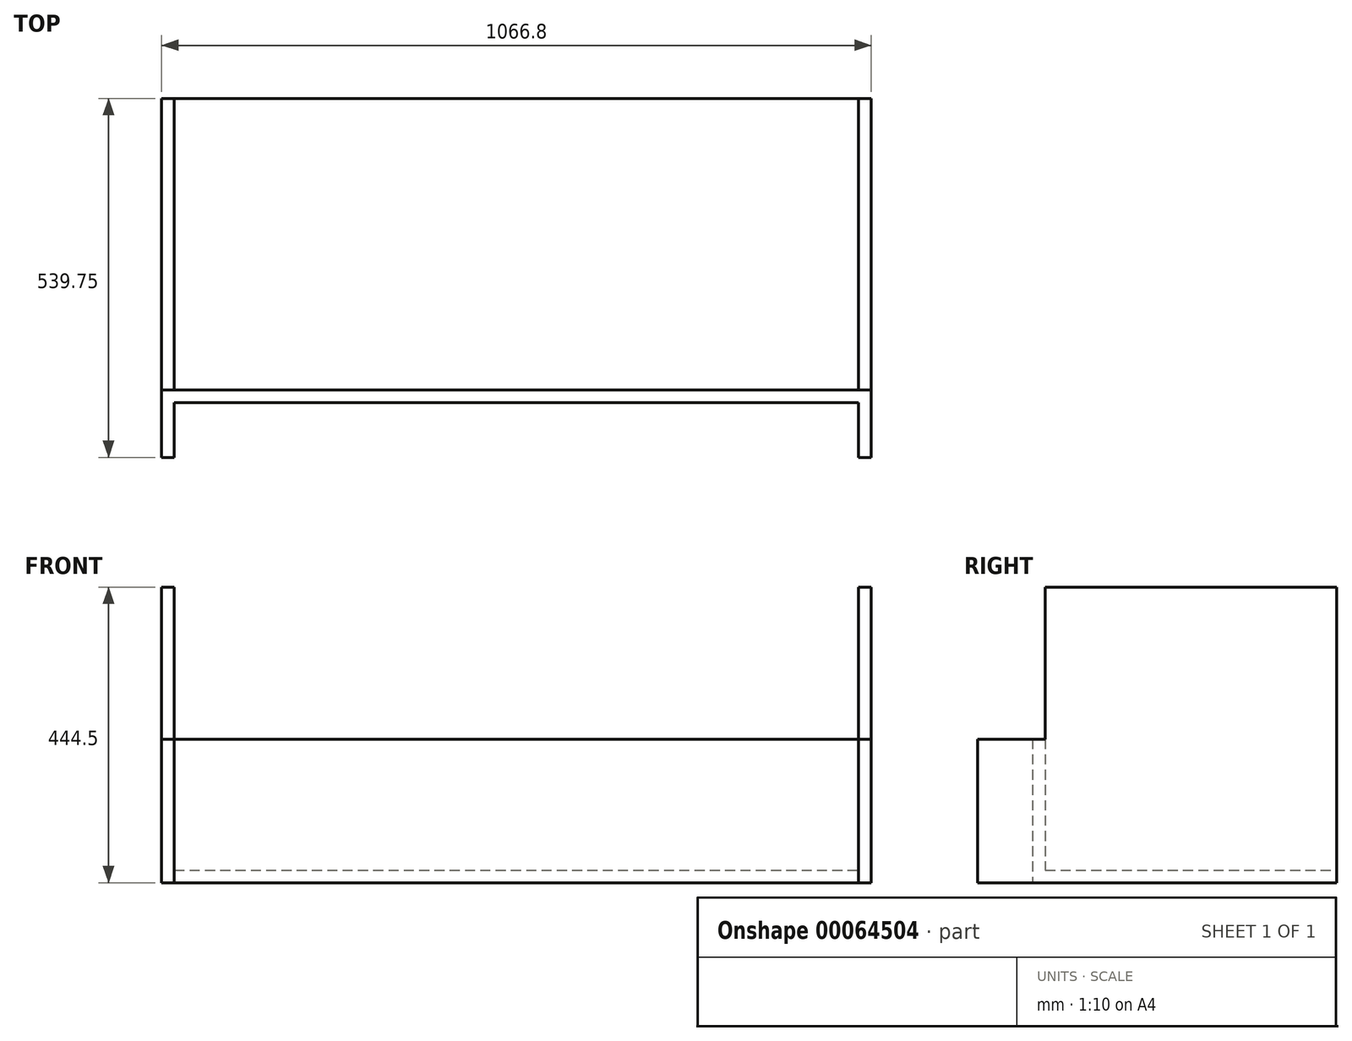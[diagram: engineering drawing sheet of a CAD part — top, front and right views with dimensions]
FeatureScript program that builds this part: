
annotation { "Feature Type Name" : "Feature", "Feature Type Description" : "" }
export const myFeature = defineFeature(function(context is Context, id is Id, definition is map)
    precondition{}
    {
        {
            var Q0;
            Q0=qCreatedBy(makeId("Top.planeOp"),FACE);
            var sketch = newSketch(context, id + "F0", { "sketchPlane" : qUnion([Q0])});
            skLineSegment(sketch, "E0.rect.bottom", {"start": v(533.4, -228.6) * mm, "end": v(-533.4, -228.6) * mm});
            skLineSegment(sketch, "E0.rect.top", {"start": v(533.4, 228.6) * mm, "end": v(-533.4, 228.6) * mm});
            skLineSegment(sketch, "E0.rect.left", {"start": v(533.4, -228.6) * mm, "end": v(533.4, 228.6) * mm});
            skLineSegment(sketch, "E0.rect.right", {"start": v(-533.4, -228.6) * mm, "end": v(-533.4, 228.6) * mm});
            skPoint(sketch, "E0.rect.middle", {"position": v(0, 0) * mm});
            skSolve(sketch);
        }
        {
            var Q0;
            Q0=makeQuery(id+"F0.imprint","IMPRINT",FACE,{"disambiguationData":[TD([[makeQuery(id+"F0.imprint","IMPRINT",EDGE,{"derivedFrom":sQuery(id+"F0.wireOp",EDGE,"E0.rect.bottom")}),-1.0]])]});
            extrude(context, id + "F1", {"entities" : qUnion([Q0]), "depth" : 19.05 * mm});
        }
        {
            var Q0;
            Q0=makeQuery(id+"F1.opExtrude","CAP_FACE",FACE,{"disambiguationData":[OSD([sQuery(id+"F0.wireOp",EDGE,"E0.rect.bottom"),sQuery(id+"F0.wireOp",EDGE,"E0.rect.top"),sQuery(id+"F0.wireOp",EDGE,"E0.rect.left"),sQuery(id+"F0.wireOp",EDGE,"E0.rect.right")])],"isStart":false});
            var sketch = newSketch(context, id + "F2", { "sketchPlane" : qUnion([Q0])});
            skLineSegment(sketch, "E1.bottom", {"start": v(-533.4, -209.55) * mm, "end": v(-514.35, -209.55) * mm});
            skLineSegment(sketch, "E1.top", {"start": v(-533.4, 228.6) * mm, "end": v(-514.35, 228.6) * mm});
            skLineSegment(sketch, "E1.left", {"start": v(-533.4, -209.55) * mm, "end": v(-533.4, 228.6) * mm});
            skLineSegment(sketch, "E1.right", {"start": v(-514.35, -209.55) * mm, "end": v(-514.35, 228.6) * mm});
            skLineSegment(sketch, "E2", {"start": v(0, -228.6) * mm, "end": v(0, 228.6) * mm, "construction": true});
            skLineSegment(sketch, "E3.MirrorCS", {"start": v(533.4, 228.6) * mm, "end": v(514.35, 228.6) * mm});
            skLineSegment(sketch, "E4.MirrorCS", {"start": v(533.4, -209.55) * mm, "end": v(514.35, -209.55) * mm});
            skLineSegment(sketch, "E5.MirrorCS", {"start": v(514.35, -209.55) * mm, "end": v(514.35, 228.6) * mm});
            skLineSegment(sketch, "E6.MirrorCS", {"start": v(533.4, -209.55) * mm, "end": v(533.4, 228.6) * mm});
            skLineSegment(sketch, "E7.bottom", {"start": v(-533.4, -228.6) * mm, "end": v(533.4, -228.6) * mm});
            skLineSegment(sketch, "E7.top", {"start": v(-533.4, -209.55) * mm, "end": v(533.4, -209.55) * mm});
            skLineSegment(sketch, "E7.left", {"start": v(-533.4, -228.6) * mm, "end": v(-533.4, -209.55) * mm});
            skLineSegment(sketch, "E7.right", {"start": v(533.4, -228.6) * mm, "end": v(533.4, -209.55) * mm});
            skSolve(sketch);
        }
        {
            var Q0;
            Q0=makeQuery(id+"F2.imprint","IMPRINT",FACE,{"disambiguationData":[TD([[makeQuery(id+"F2.imprint","IMPRINT",EDGE,{"derivedFrom":sQuery(id+"F2.wireOp",EDGE,"E3.MirrorCS")}),1.0]])]});
            var Q1;
            Q1=makeQuery(id+"F2.imprint","IMPRINT",FACE,{"disambiguationData":[TD([[makeQuery(id+"F2.imprint","IMPRINT",EDGE,{"derivedFrom":sQuery(id+"F2.wireOp",EDGE,"E1.top")}),1.0]])]});
            extrude(context, id + "F3", {"entities" : qUnion([Q0, Q1]), "operationType" : NewBodyOperationType.ADD, "depth" : 425.45 * mm});
        }
        {
            var Q0;
            Q0=makeQuery(id+"F2.imprint","IMPRINT",FACE,{"disambiguationData":[TD([[makeQuery(id+"F2.imprint","IMPRINT",EDGE,{"derivedFrom":sQuery(id+"F2.wireOp",EDGE,"E7.bottom")}),-1.0]])]});
            extrude(context, id + "F4", {"entities" : qUnion([Q0]), "operationType" : NewBodyOperationType.ADD, "depth" : 196.85 * mm});
        }
        {
            var Q0;
            Q0=makeQuery(id+"F4.boolean.opBoolean","MERGE",FACE,{"derivedFrom":[makeQuery(id+"F1.opExtrude","SWEPT_FACE",FACE,{"disambiguationData":[OSD([sQuery(id+"F0.wireOp",EDGE,"E0.rect.bottom")])]}),makeQuery(id+"F4.opExtrude","SWEPT_FACE",FACE,{"disambiguationData":[OSD([sQuery(id+"F2.wireOp",EDGE,"E7.bottom")])]})]});
            var sketch = newSketch(context, id + "F5", { "sketchPlane" : qUnion([Q0])});
            skSolve(sketch);
        }
        {
            var Q0;
            {var subQ0=sQuery(id+"F0.wireOp",EDGE,"E0.rect.bottom");Q0=makeQuery(id+"F5.imprint","IMPRINT",FACE,{"disambiguationData":[TD([[makeQuery(id+"F5.imprint","IMPRINT",EDGE,{"derivedFrom":makeQuery(id+"F1.opExtrude","CAP_EDGE",EDGE,{"disambiguationData":[OSD([subQ0])],"isStart":true})}),-1.0]])]});}
            var sketch = newSketch(context, id + "F6", { "sketchPlane" : qUnion([Q0])});
            skLineSegment(sketch, "E8.bottom", {"start": v(-533.4, 215.9) * mm, "end": v(-514.35, 215.9) * mm});
            skLineSegment(sketch, "E8.top", {"start": v(-533.4, 0) * mm, "end": v(-514.35, 0) * mm});
            skLineSegment(sketch, "E8.left", {"start": v(-533.4, 215.9) * mm, "end": v(-533.4, 0) * mm});
            skLineSegment(sketch, "E8.right", {"start": v(-514.35, 215.9) * mm, "end": v(-514.35, 0) * mm});
            skLineSegment(sketch, "E9.bottom", {"start": v(533.4, 215.9) * mm, "end": v(514.35, 215.9) * mm});
            skLineSegment(sketch, "E9.top", {"start": v(533.4, 0) * mm, "end": v(514.35, 0) * mm});
            skLineSegment(sketch, "E9.left", {"start": v(533.4, 215.9) * mm, "end": v(533.4, 0) * mm});
            skLineSegment(sketch, "E9.right", {"start": v(514.35, 215.9) * mm, "end": v(514.35, 0) * mm});
            skSolve(sketch);
        }
        {
            var Q0;
            Q0 = qSketchRegion(id + "F6", true);
            extrude(context, id + "F7", {"entities" : qUnion([Q0]), "operationType" : NewBodyOperationType.ADD, "depth" : 82.55 * mm});
        }
    });
